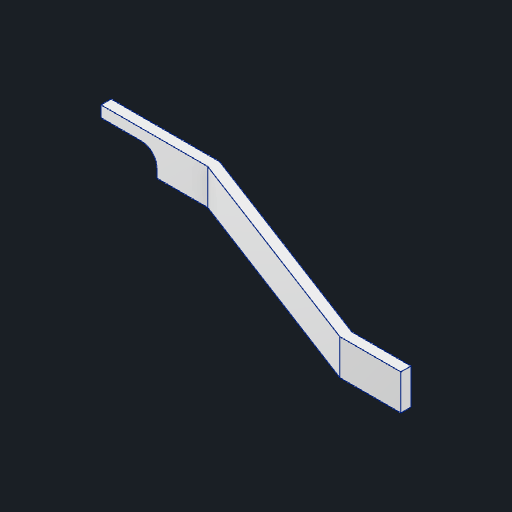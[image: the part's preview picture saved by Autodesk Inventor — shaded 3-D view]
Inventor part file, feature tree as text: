
AUTODESK INVENTOR PART (.ipt)
format: ipt  version: 2024 (Build 280153000, 153)  size: 261,632 bytes
history: native  units: mm
features: extrude x2, sketch x2, fillet x1
ambient origin geometry x8: Origin, YZ Plane, XZ Plane, XY Plane, X Axis, Y Axis, Z Axis, Center Point
bodies: Solid1 (feature_tree)
feature tree (5):
  extrude  "Extrusion1"  Depth=449.444101mm
  extrude  "Extrusion2"  Depth=30.0mm
  fillet  "Fillet1"  Radius=27.776137mm
  sketch  "Sketch1"  dims[d2=100.0mm d3=449.444101mm]
  sketch  "Sketch2"  dims[d4=120.0mm d5=27.776137mm d6=27.776137mm d7=20.0mm d8=70.0mm d9=0.0mm d10=110.0mm d11=0.0mm d12=30.0mm]
